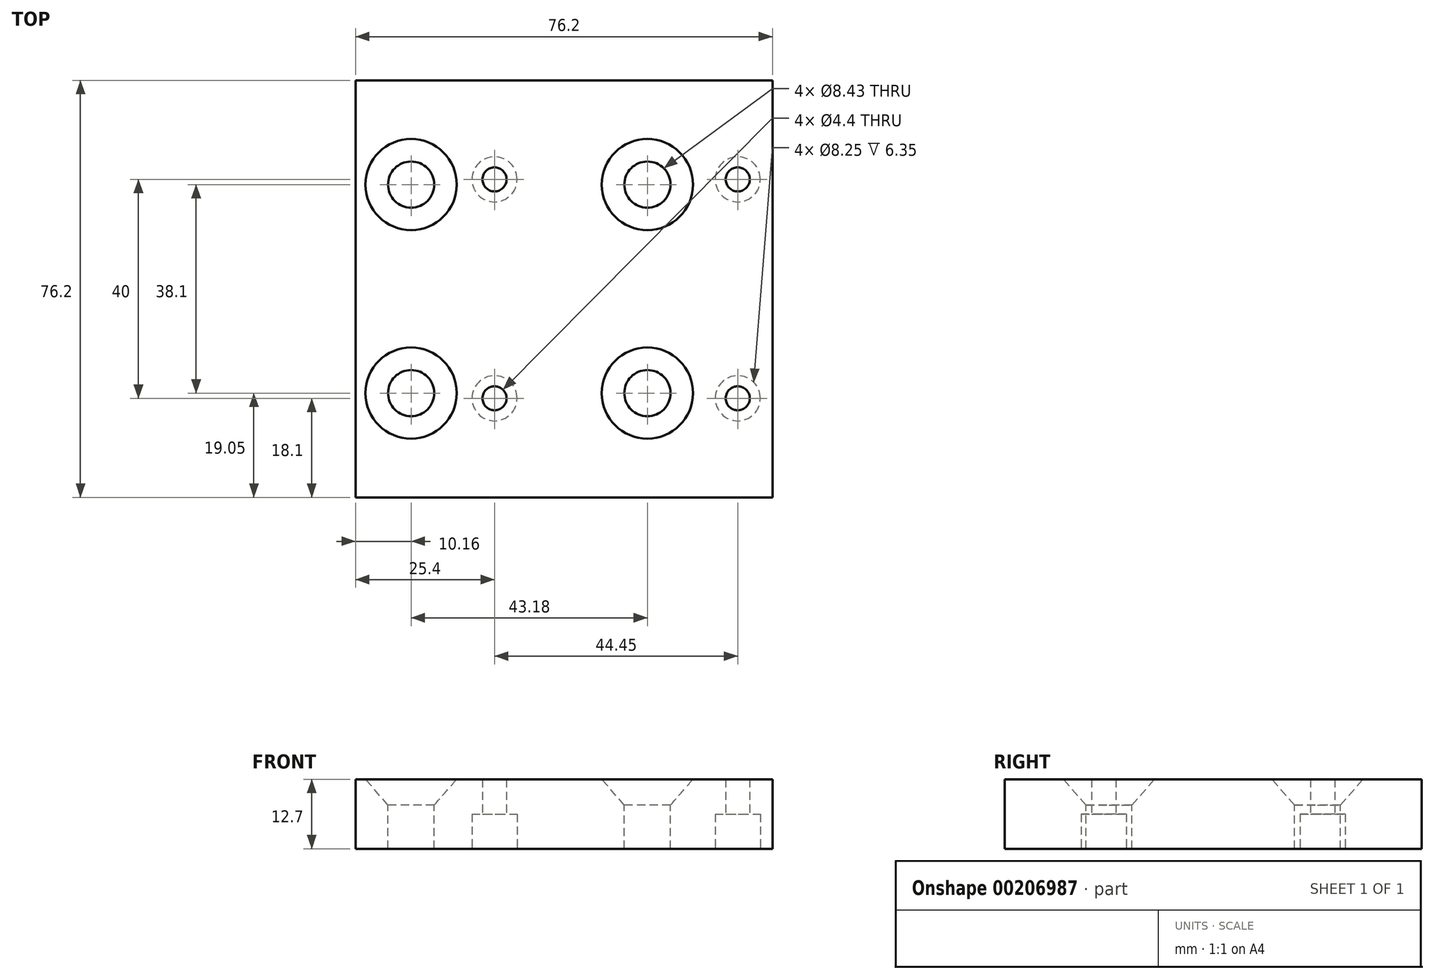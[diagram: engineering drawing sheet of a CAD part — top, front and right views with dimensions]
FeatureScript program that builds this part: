
annotation { "Feature Type Name" : "Feature", "Feature Type Description" : "" }
export const myFeature = defineFeature(function(context is Context, id is Id, definition is map)
    precondition{}
    {
        {
            var Q0;
            Q0=qCreatedBy(makeId("Top.planeOp"),FACE);
            var sketch = newSketch(context, id + "F0", { "sketchPlane" : qUnion([Q0])});
            skLineSegment(sketch, "E0.bottom", {"start": v(38.1, -38.1) * mm, "end": v(-38.1, -38.1) * mm});
            skLineSegment(sketch, "E0.top", {"start": v(38.1, 38.1) * mm, "end": v(-38.1, 38.1) * mm});
            skLineSegment(sketch, "E0.left", {"start": v(38.1, -38.1) * mm, "end": v(38.1, 38.1) * mm});
            skLineSegment(sketch, "E0.right", {"start": v(-38.1, -38.1) * mm, "end": v(-38.1, 38.1) * mm});
            skPoint(sketch, "E0.middle", {"position": v(0, 0) * mm});
            skSolve(sketch);
        }
        {
            var Q0;
            Q0 = qSketchRegion(id + "F0", true);
            extrude(context, id + "F1", {"entities" : qUnion([Q0]), "endBound" : BoundingType.SYMMETRIC, "depth" : 12.7 * mm});
        }
        {
            var Q0;
            Q0=makeQuery(id+"F1.opExtrude","CAP_FACE",FACE,{"disambiguationData":[OSD([sQuery(id+"F0.wireOp",EDGE,"E0.bottom"),sQuery(id+"F0.wireOp",EDGE,"E0.top"),sQuery(id+"F0.wireOp",EDGE,"E0.left"),sQuery(id+"F0.wireOp",EDGE,"E0.right")])],"isStart":false});
            var sketch = newSketch(context, id + "F2", { "sketchPlane" : qUnion([Q0])});
            skPoint(sketch, "E1", {"position": v(-27.94, 19.05) * mm});
            skPoint(sketch, "E2", {"position": v(15.24, 19.05) * mm});
            skPoint(sketch, "E3", {"position": v(15.24, -19.05) * mm});
            skPoint(sketch, "E4", {"position": v(-27.94, -19.05) * mm});
            skSolve(sketch);
        }
        {
            var Q0;
            Q0=sQuery(id+"F2.wireOp",VERTEX,"E1");
            var Q1;
            Q1=sQuery(id+"F2.wireOp",VERTEX,"E2");
            var Q2;
            Q2=sQuery(id+"F2.wireOp",VERTEX,"E3");
            var Q3;
            Q3=sQuery(id+"F2.wireOp",VERTEX,"E4");
            var Q4;
            Q4=makeQuery(id+"F1.opExtrude","SWEPT_BODY",BODY,{"disambiguationData":[OSD([sQuery(id+"F0.wireOp",EDGE,"E0.bottom"),sQuery(id+"F0.wireOp",EDGE,"E0.top"),sQuery(id+"F0.wireOp",EDGE,"E0.left"),sQuery(id+"F0.wireOp",EDGE,"E0.right")])]});
            hole(context, id + "F3", {"style" : HoleStyle.C_SINK, "endStyle" : HoleEndStyle.THROUGH, "standardTappedOrClearance" : lookupTablePath({ "standard" : "ANSI", "fit" : "Normal (ASME)", "size" : "5/16", "type" : "Clearance" }), "standardBlindInLast" : lookupTablePath({ "fit" : "Free", "standard" : "ANSI", "size" : "5/16", "type" : "Clearance" }), "holeDiameter" : 8.43 * mm, "cSinkDiameter" : 16.66 * mm, "cSinkAngle" : 82 * degree, "startFromSketch" : true, "locations" : qUnion([Q0, Q1, Q2, Q3]), "scope" : qUnion([Q4]), "isTappedThrough" : true});
        }
        {
            var Q0;
            Q0=makeQuery(id+"F1.opExtrude","CAP_FACE",FACE,{"disambiguationData":[OSD([sQuery(id+"F0.wireOp",EDGE,"E0.bottom"),sQuery(id+"F0.wireOp",EDGE,"E0.top"),sQuery(id+"F0.wireOp",EDGE,"E0.left"),sQuery(id+"F0.wireOp",EDGE,"E0.right")])],"isStart":true});
            var sketch = newSketch(context, id + "F4", { "sketchPlane" : qUnion([Q0])});
            skPoint(sketch, "E5", {"position": v(-12.7, 20) * mm});
            skPoint(sketch, "E6", {"position": v(31.75, 20) * mm});
            skPoint(sketch, "E7", {"position": v(31.75, -20) * mm});
            skPoint(sketch, "E8", {"position": v(-12.7, -20) * mm});
            skSolve(sketch);
        }
        {
            var Q0;
            Q0=sQuery(id+"F4.wireOp",VERTEX,"E5");
            var Q1;
            Q1=sQuery(id+"F4.wireOp",VERTEX,"E6");
            var Q2;
            Q2=sQuery(id+"F4.wireOp",VERTEX,"E7");
            var Q3;
            Q3=sQuery(id+"F4.wireOp",VERTEX,"E8");
            var Q4;
            Q4=makeQuery(id+"F1.opExtrude","SWEPT_BODY",BODY,{"disambiguationData":[OSD([sQuery(id+"F0.wireOp",EDGE,"E0.bottom"),sQuery(id+"F0.wireOp",EDGE,"E0.top"),sQuery(id+"F0.wireOp",EDGE,"E0.left"),sQuery(id+"F0.wireOp",EDGE,"E0.right")])]});
            hole(context, id + "F5", {"style" : HoleStyle.C_BORE, "endStyle" : HoleEndStyle.THROUGH, "holeDiameter" : 4.4 * mm, "cBoreDiameter" : 8.25 * mm, "cBoreDepth" : 6.35 * mm, "startFromSketch" : true, "locations" : qUnion([Q0, Q1, Q2, Q3]), "scope" : qUnion([Q4]), "isTappedThrough" : true});
        }
    });
